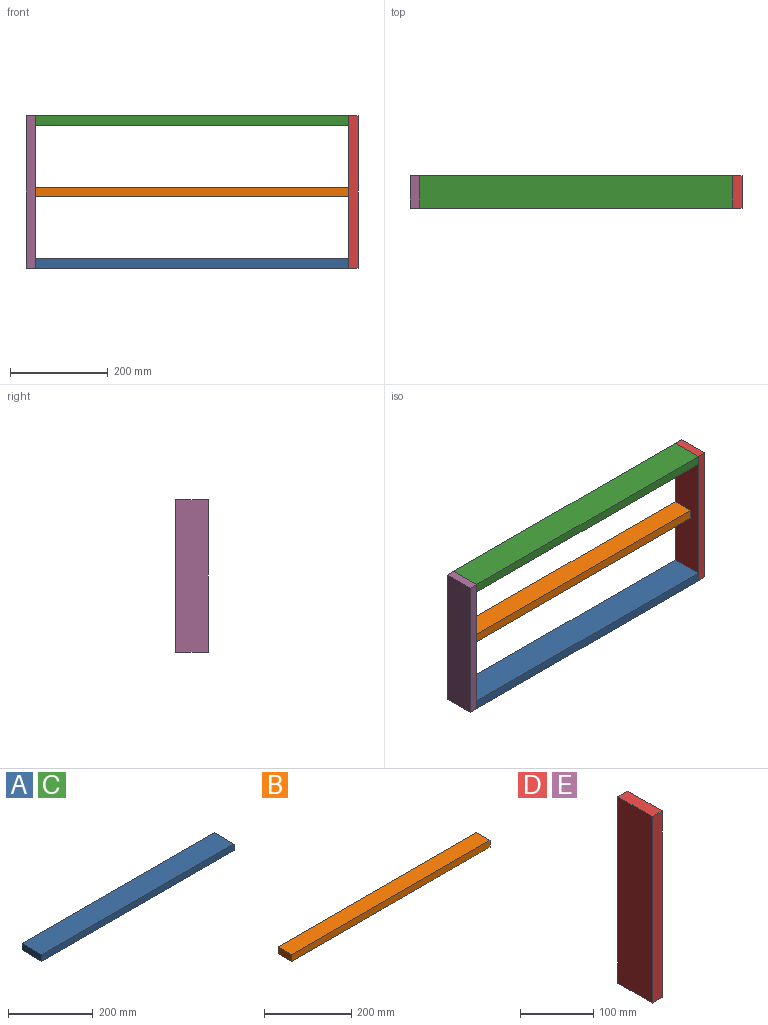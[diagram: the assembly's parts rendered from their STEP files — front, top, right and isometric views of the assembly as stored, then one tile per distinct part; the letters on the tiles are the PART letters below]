
ASSEMBLY  parts=5 mates=4
PART A: 6 faces, bbox 641.4x66.7x19.1 mm
  f0: plane 66.68x19.05mm, normal (-1,0,0), area 1270.2mm2, adj f1,f3,f4,f5
  f1: plane 641.35x66.68mm, normal (0,0,-1), area 42762mm2, adj f0,f2,f4,f5
  f2: plane 66.68x19.05mm, normal (1,0,0), area 1270.2mm2, adj f1,f3,f4,f5
  f3: plane 641.35x66.68mm, normal (0,0,1), area 42762mm2, adj f0,f2,f4,f5
  f4: plane 641.35x19.05mm, normal (0,-1,0), area 12217.7mm2, adj f0,f1,f2,f3
  f5: plane 641.35x19.05mm, normal (0,1,0), area 12217.7mm2, adj f0,f1,f2,f3
PART B: 6 faces, bbox 641.4x44.5x19.1 mm
  f0: plane 44.45x19.05mm, normal (-1,0,0), area 846.8mm2, adj f1,f3,f4,f5
  f1: plane 641.35x44.45mm, normal (0,0,-1), area 28508mm2, adj f0,f2,f4,f5
  f2: plane 44.45x19.05mm, normal (1,0,0), area 846.8mm2, adj f1,f3,f4,f5
  f3: plane 641.35x44.45mm, normal (0,0,1), area 28508mm2, adj f0,f2,f4,f5
  f4: plane 641.35x19.05mm, normal (0,-1,0), area 12217.7mm2, adj f0,f1,f2,f3
  f5: plane 641.35x19.05mm, normal (0,1,0), area 12217.7mm2, adj f0,f1,f2,f3
PART C: same geometry as A
PART D: 6 faces, bbox 19.1x66.7x311.2 mm
  f0: plane 311.15x66.68mm, normal (1,0,0), area 20745.9mm2, adj f1,f3,f4,f5
  f1: plane 66.68x19.05mm, normal (0,0,1), area 1270.2mm2, adj f0,f2,f4,f5
  f2: plane 311.15x66.68mm, normal (-1,0,0), area 20745.9mm2, adj f1,f3,f4,f5
  f3: plane 66.68x19.05mm, normal (0,0,-1), area 1270.2mm2, adj f0,f2,f4,f5
  f4: plane 311.15x19.05mm, normal (0,-1,0), area 5927.4mm2, adj f0,f1,f2,f3
  f5: plane 311.15x19.05mm, normal (0,1,0), area 5927.4mm2, adj f0,f1,f2,f3
PART E: same geometry as D
PLACE A t=(-42.16,0,-292.1)mm
PLACE B t=(-42.16,0,0)mm
PLACE C t=(-42.16,0,0)mm
PLACE D t=(618.24,0,0)mm
PLACE E t=(-42.16,0,0)mm
MATE fastened A.f0 <-> E.f0  axis (-1,0,0) through (-23.11,-33.34,0)mm
MATE fastened C.f0 <-> E.f0  axis (-1,0,0) through (-23.11,-33.34,311.15)mm
MATE fastened D.f2 <-> C.f2  axis (-1,0,0) through (618.24,-33.34,311.15)mm
MATE fastened B.f0 <-> E.f0  axis (-1,0,0) through (-23.11,0,155.57)mm
